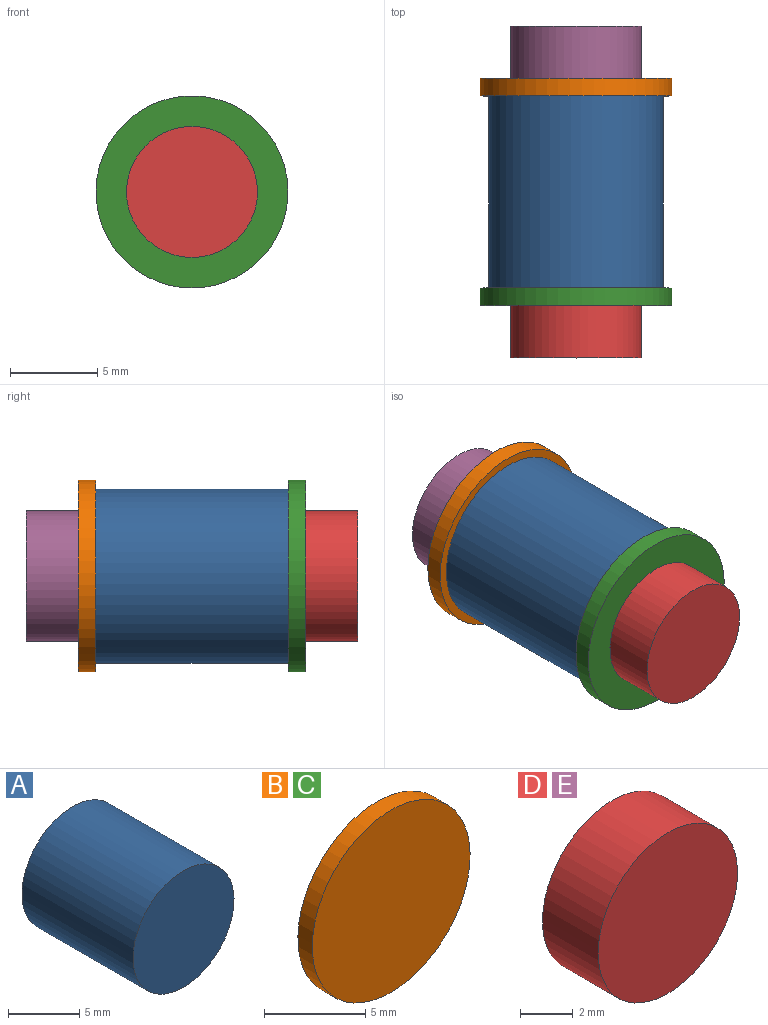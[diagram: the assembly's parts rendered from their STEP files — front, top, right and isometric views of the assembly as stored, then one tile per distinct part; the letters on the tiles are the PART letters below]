
ASSEMBLY  parts=5 mates=4
PART A: 3 faces, bbox 10x11x10 mm
  f0: cylinder r=5mm len=11mm, axis (0,1,0), area 345.6mm2, adj f1,f2
  f1: plane 10x10mm, normal (0,-1,0), area 78.5mm2, adj f0
  f2: plane 10x10mm, normal (0,1,0), area 78.5mm2, adj f0
PART B: 3 faces, bbox 11x1x11 mm
  f0: cylinder r=5.5mm len=11mm, axis (0,1,0), area 34.6mm2, adj f1,f2
  f1: plane 11x11mm, normal (0,-1,0), area 95mm2, adj f0
  f2: plane 11x11mm, normal (0,1,0), area 95mm2, adj f0
PART C: same geometry as B
PART D: 3 faces, bbox 7.5x3x7.5 mm
  f0: cylinder r=3.75mm len=7.5mm, axis (0,1,0), area 70.7mm2, adj f1,f2
  f1: plane 7.5x7.5mm, normal (0,-1,0), area 44.2mm2, adj f0
  f2: plane 7.5x7.5mm, normal (0,1,0), area 44.2mm2, adj f0
PART E: same geometry as D
PLACE A t=(0,-1,0.49)mm
PLACE B at identity
PLACE C t=(0,-12,0)mm
PLACE D t=(0,-13,0.49)mm
PLACE E t=(0,3,0.49)mm
MATE planar E.f0 <-> B.f0  axis (0,-1,0) through (0,0,0.49)mm
MATE planar A.f0 <-> B.f0  axis (0,1,0) through (0,-1,0.49)mm
MATE planar D.f0 <-> C.f0  axis (0,1,0) through (0,-13,0.49)mm
MATE planar C.f0 <-> A.f0  axis (0,1,0) through (0,-12,0.49)mm
